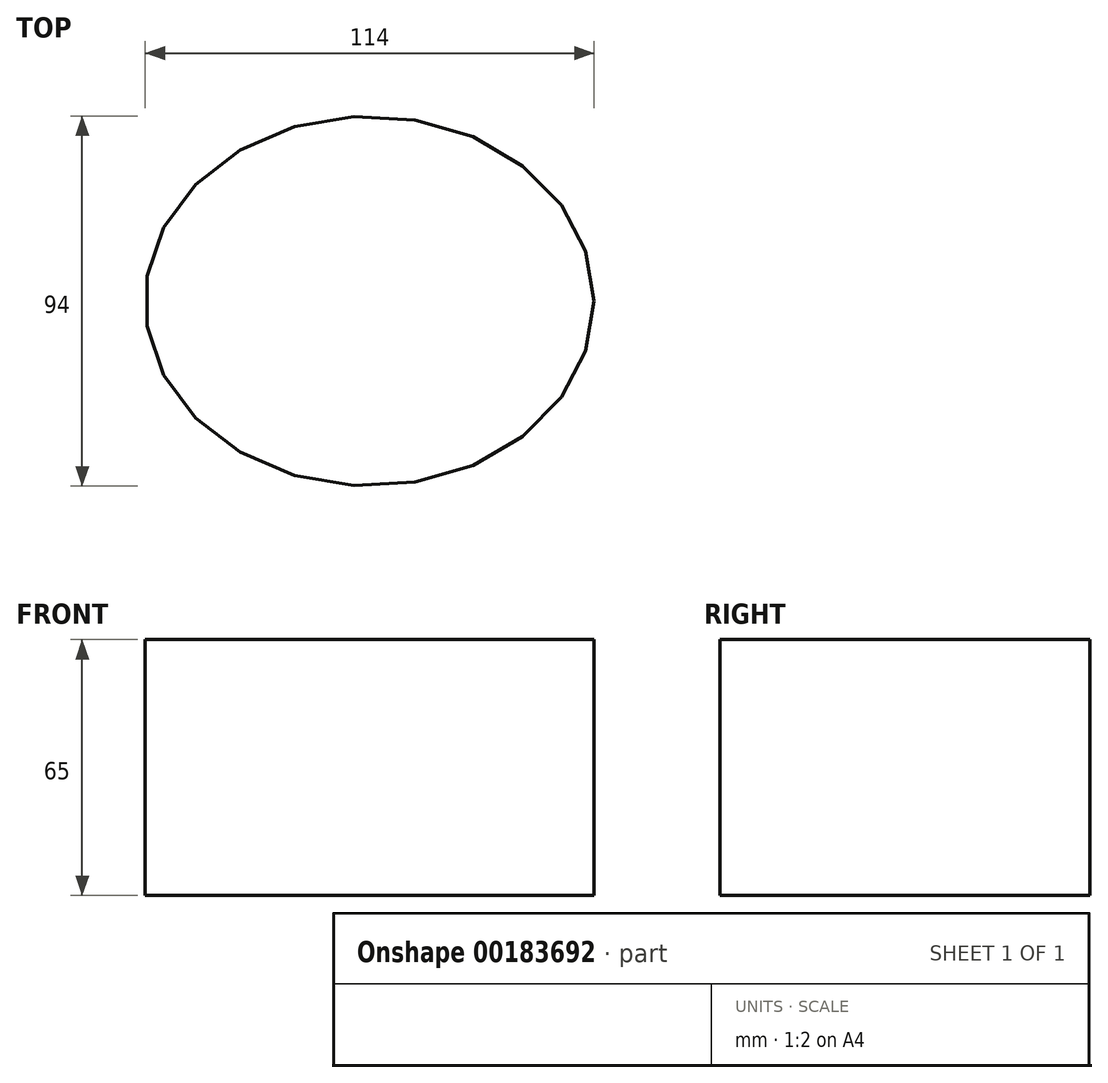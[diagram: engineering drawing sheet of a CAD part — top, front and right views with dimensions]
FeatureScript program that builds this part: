
annotation { "Feature Type Name" : "Feature", "Feature Type Description" : "" }
export const myFeature = defineFeature(function(context is Context, id is Id, definition is map)
    precondition{}
    {
        {
            var Q0;
            Q0=qCreatedBy(makeId("Top.planeOp"),FACE);
            var sketch = newSketch(context, id + "F0", { "sketchPlane" : qUnion([Q0])});
            skEllipse(sketch, "E0", {"center": v(0, 0) * mm, "majorRadius": 57 * mm, "minorRadius": 47 * mm, "majorAxis": v(1, 0)});
            skFitSpline(sketch, "E1.0", {"points": [v(54.96, -2.21) * mm, v(55.02, 0) * mm, v(54.96, 2.21) * mm, v(54.7, 5.14) * mm, v(54.04, 8.76) * mm, v(52.74, 13) * mm, v(50.95, 17.11) * mm, v(48.68, 21.08) * mm, v(45.94, 24.85) * mm, v(43.28, 27.82) * mm, v(40.93, 30.08) * mm, v(39.05, 31.7) * mm, v(37.07, 33.25) * mm, v(34.33, 35.2) * mm, v(30.7, 37.41) * mm, v(26.08, 39.7) * mm, v(21.2, 41.6) * mm, v(16.12, 43.1) * mm, v(10.87, 44.19) * mm, v(6.38, 44.74) * mm, v(2.75, 44.96) * mm, v(0, 45.02) * mm, v(-2.75, 44.96) * mm, v(-6.38, 44.74) * mm, v(-10.87, 44.19) * mm, v(-16.12, 43.1) * mm, v(-21.2, 41.6) * mm, v(-26.08, 39.7) * mm, v(-30.7, 37.41) * mm, v(-34.33, 35.2) * mm, v(-37.07, 33.25) * mm, v(-39.05, 31.7) * mm, v(-40.93, 30.08) * mm, v(-43.28, 27.82) * mm, v(-45.94, 24.85) * mm, v(-48.68, 21.08) * mm, v(-50.95, 17.11) * mm, v(-52.74, 13) * mm, v(-54.04, 8.76) * mm, v(-54.7, 5.14) * mm, v(-54.96, 2.21) * mm, v(-55.02, 0) * mm, v(-54.96, -2.21) * mm, v(-54.7, -5.14) * mm, v(-54.04, -8.76) * mm, v(-52.74, -13) * mm, v(-50.95, -17.11) * mm, v(-48.68, -21.08) * mm, v(-45.94, -24.85) * mm, v(-43.28, -27.82) * mm, v(-40.93, -30.08) * mm, v(-39.05, -31.7) * mm, v(-37.07, -33.25) * mm, v(-34.33, -35.2) * mm, v(-30.7, -37.41) * mm, v(-26.08, -39.7) * mm, v(-21.2, -41.6) * mm, v(-16.12, -43.1) * mm, v(-10.87, -44.19) * mm, v(-6.38, -44.74) * mm, v(-2.75, -44.96) * mm, v(0, -45.02) * mm, v(2.75, -44.96) * mm, v(6.38, -44.74) * mm, v(10.87, -44.19) * mm, v(16.12, -43.1) * mm, v(21.2, -41.6) * mm, v(26.08, -39.7) * mm, v(30.7, -37.41) * mm, v(34.33, -35.2) * mm, v(37.07, -33.25) * mm, v(39.05, -31.7) * mm, v(40.93, -30.08) * mm, v(43.28, -27.82) * mm, v(45.94, -24.85) * mm, v(48.68, -21.08) * mm, v(50.95, -17.11) * mm, v(52.74, -13) * mm, v(54.04, -8.76) * mm, v(54.7, -5.14) * mm, v(54.96, -2.21) * mm, v(55.02, 0) * mm, v(54.96, 2.21) * mm, v(54.96, -2.21) * mm]});
            skSolve(sketch);
        }
        {
            var Q0;
            Q0 = qSketchRegion(id + "F0", true);
            extrude(context, id + "F1", {"entities" : qUnion([Q0]), "depth" : 65 * mm});
        }
    });
